# Revit family: Sink_Kitchen_Abey_Builders_SingleBowl_Overflow_FaceBased
name_source: partatom
category: Plumbing Fixtures
units: mm (PartAtom-declared; Revit-internal decimal feet)

## family parameters
Cut with Voids When Loaded = Yes
Host = Face
Maintain Annotation Orientation = No
OmniClass Number = 23.31.13.00
OmniClass Title = Sinks
Part Type = Normal
Room Calculation Point = No
Round Connector Dimension = Use Diameter
Shared = No

## types (1)
- CUA340-12
    Assembly Code = D2010410
    BodyMaterial = Metal_Abey_StainlessSteel
    CW Connection = No
    Cost = 0 $
    Default Elevation = 900 mm
    Description = Abey CUA Single Bowl Kitchen Sink
    HW Connection = No
    IfcExportAs = IfcSanitaryTerminal
    IfcExportType = SINK
    Manufacturer = Abey
    ManufacturerOverallDepth = 440 mm
    ManufacturerOverallHeight = 200 mm
    ManufacturerOverallWidth = 380 mm
    ManufacturerSpecCode = CUA340-12
    ManufacturerURLProductSpecific = https://www.abeyspecifier.com.au
    Model = CUA340-12
    ModifiedIssue = 20251103 $
    PopOutMaterial = Metal_Abey_StainlessSteel
    Type Comments = Sink - Kitchen - Single Bowl - Overflow - Double Bowl Kitchen Sink
    URL = https://www.abey.com.au
    Uniclass2015Code = Pr_40_20_96_45
    Uniclass2015Title = Kitchen sinks
    Uniclass2015Version = Products v1.38
    Vent Connection = No
    Waste Connection = Yes

## geometry (parser evidence)
native form markers: Sweep x6
no freeform markers — native parametric forms only
